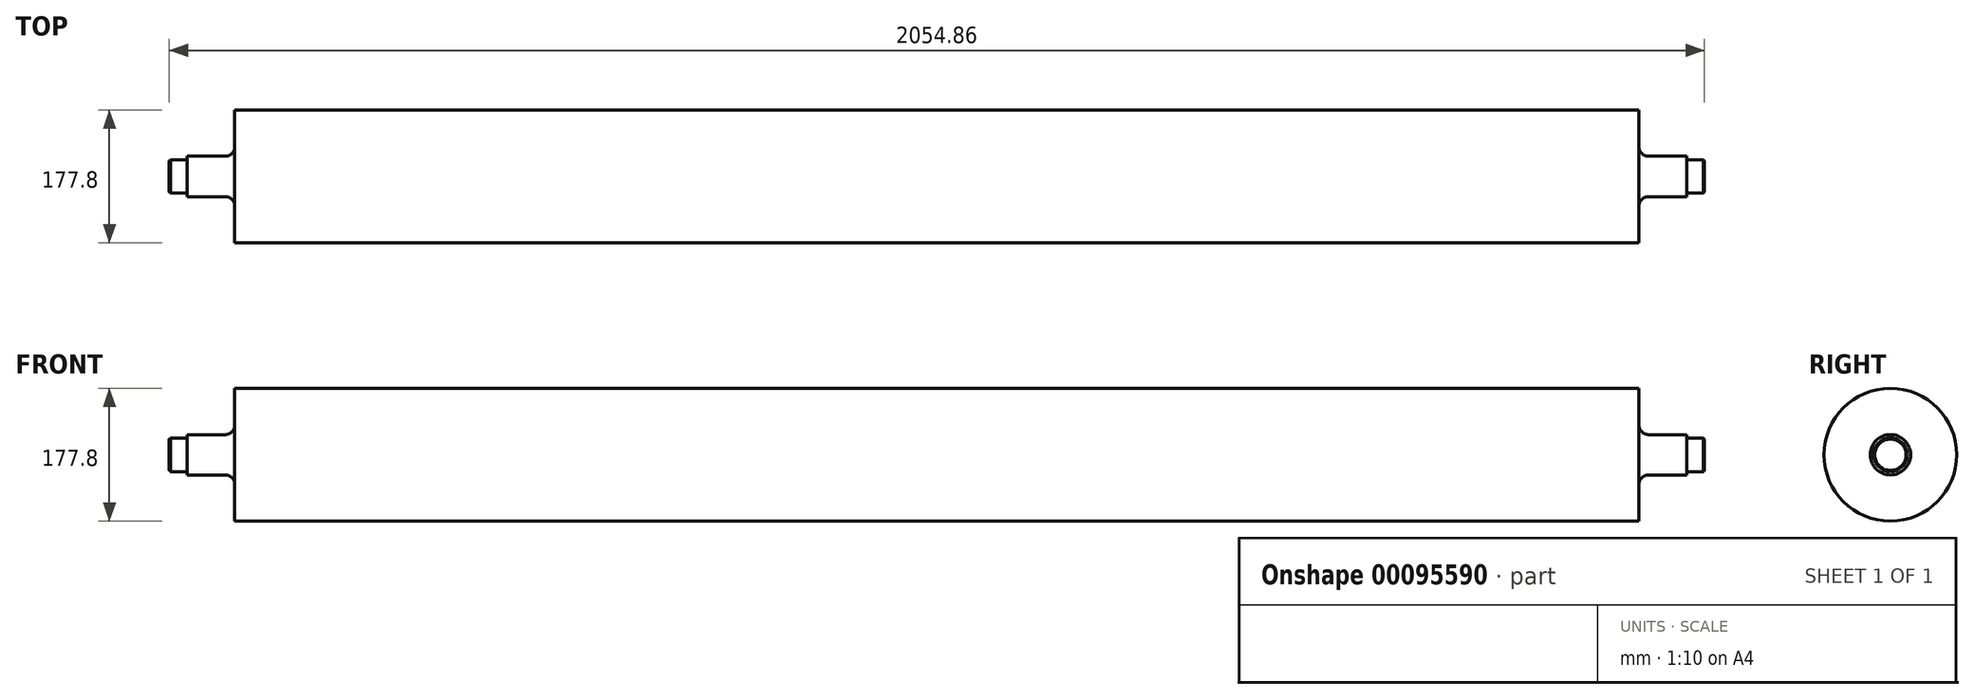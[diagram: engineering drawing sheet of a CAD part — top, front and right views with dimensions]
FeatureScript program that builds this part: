
annotation { "Feature Type Name" : "Feature", "Feature Type Description" : "" }
export const myFeature = defineFeature(function(context is Context, id is Id, definition is map)
    precondition{}
    {
        {
            var Q0;
            Q0=qCreatedBy(makeId("Right.planeOp"),FACE);
            var sketch = newSketch(context, id + "F0", { "sketchPlane" : qUnion([Q0])});
            skCircle(sketch, "E0", {"center": v(0, 0) * mm, "radius": 22.51 * mm});
            skSolve(sketch);
        }
        {
            var Q0;
            Q0 = qSketchRegion(id + "F0", true);
            extrude(context, id + "F1", {"entities" : qUnion([Q0]), "endBound" : BoundingType.SYMMETRIC, "depth" : 2054.86 * mm});
        }
        {
            var Q0;
            Q0=qCreatedBy(makeId("Right.planeOp"),FACE);
            var sketch = newSketch(context, id + "F2", { "sketchPlane" : qUnion([Q0])});
            skCircle(sketch, "E1", {"center": v(0, 0) * mm, "radius": 27 * mm});
            skSolve(sketch);
        }
        {
            var Q0;
            Q0 = qSketchRegion(id + "F2", true);
            extrude(context, id + "F3", {"entities" : qUnion([Q0]), "operationType" : NewBodyOperationType.ADD, "endBound" : BoundingType.SYMMETRIC, "depth" : 2007.1 * mm});
        }
        {
            var Q0;
            Q0=qCreatedBy(makeId("Right.planeOp"),FACE);
            var sketch = newSketch(context, id + "F4", { "sketchPlane" : qUnion([Q0])});
            skCircle(sketch, "E2", {"center": v(0, 0) * mm, "radius": 88.9 * mm});
            skSolve(sketch);
        }
        {
            var Q0;
            Q0 = qSketchRegion(id + "F4", true);
            extrude(context, id + "F5", {"entities" : qUnion([Q0]), "operationType" : NewBodyOperationType.ADD, "endBound" : BoundingType.SYMMETRIC, "depth" : 1879.6 * mm});
        }
        {
            var Q0;
            Q0=makeQuery(id+"F5.boolean.opBoolean","INTERSECT",EDGE,{"derivedFrom":[makeQuery(id+"F3.opExtrude","SWEPT_FACE",FACE,{"disambiguationData":[OSD([sQuery(id+"F2.wireOp",EDGE,"E1")])]}),makeQuery(id+"F5.opExtrude","CAP_FACE",FACE,{"disambiguationData":[OSD([sQuery(id+"F4.wireOp",EDGE,"E2")])],"isStart":false})]});
            var Q1;
            Q1=makeQuery(id+"F5.boolean.opBoolean","INTERSECT",EDGE,{"derivedFrom":[makeQuery(id+"F3.opExtrude","SWEPT_FACE",FACE,{"disambiguationData":[OSD([sQuery(id+"F2.wireOp",EDGE,"E1")])]}),makeQuery(id+"F5.opExtrude","CAP_FACE",FACE,{"disambiguationData":[OSD([sQuery(id+"F4.wireOp",EDGE,"E2")])],"isStart":true})]});
            fillet(context, id + "F6", {"entities" : qUnion([Q0, Q1]), "radius" : 12.7 * mm, "tangentPropagation" : true, "allowEdgeOverflow" : false});
        }
        {
            var Q0;
            Q0=makeQuery(id+"F3.boolean.opBoolean","INTERSECT",EDGE,{"derivedFrom":[makeQuery(id+"F1.opExtrude","SWEPT_FACE",FACE,{"disambiguationData":[OSD([sQuery(id+"F0.wireOp",EDGE,"E0")])]}),makeQuery(id+"F3.opExtrude","CAP_FACE",FACE,{"disambiguationData":[OSD([sQuery(id+"F2.wireOp",EDGE,"E1")])],"isStart":true})]});
            fillet(context, id + "F7", {"entities" : qUnion([Q0]), "radius" : 0.76 * mm, "tangentPropagation" : true, "allowEdgeOverflow" : false});
        }
        {
            var Q0;
            Q0=makeQuery(id+"F3.boolean.opBoolean","INTERSECT",EDGE,{"derivedFrom":[makeQuery(id+"F1.opExtrude","SWEPT_FACE",FACE,{"disambiguationData":[OSD([sQuery(id+"F0.wireOp",EDGE,"E0")])]}),makeQuery(id+"F3.opExtrude","CAP_FACE",FACE,{"disambiguationData":[OSD([sQuery(id+"F2.wireOp",EDGE,"E1")])],"isStart":false})]});
            fillet(context, id + "F8", {"entities" : qUnion([Q0]), "radius" : 0.76 * mm, "tangentPropagation" : true, "allowEdgeOverflow" : false});
        }
        {
            var Q0;
            Q0=makeQuery(id+"F1.opExtrude","CAP_FACE",FACE,{"disambiguationData":[OSD([sQuery(id+"F0.wireOp",EDGE,"E0")])],"isStart":false});
            var Q1;
            Q1=makeQuery(id+"F1.opExtrude","CAP_FACE",FACE,{"disambiguationData":[OSD([sQuery(id+"F0.wireOp",EDGE,"E0")])],"isStart":true});
            chamfer(context, id + "F9", {"entities" : qUnion([Q0, Q1]), "width" : 1.52 * mm, "tangentPropagation" : true});
        }
    });
